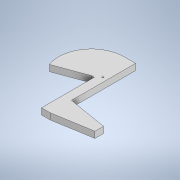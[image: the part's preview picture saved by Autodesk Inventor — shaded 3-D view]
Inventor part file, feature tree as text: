
AUTODESK INVENTOR PART (.ipt)
format: ipt  version: 2020 (Build 240168000, 168)  size: 114,688 bytes
history: native  units: mm
features: extrude x1, sketch x1
ambient origin geometry x8: Origin, YZ Plane, XZ Plane, XY Plane, X Axis, Y Axis, Z Axis, Center Point
bodies: Solide1 (feature_tree)
feature tree (2):
  extrude  "Extrusion1"  Depth=30.0mm
  sketch  "Esquisse1"
